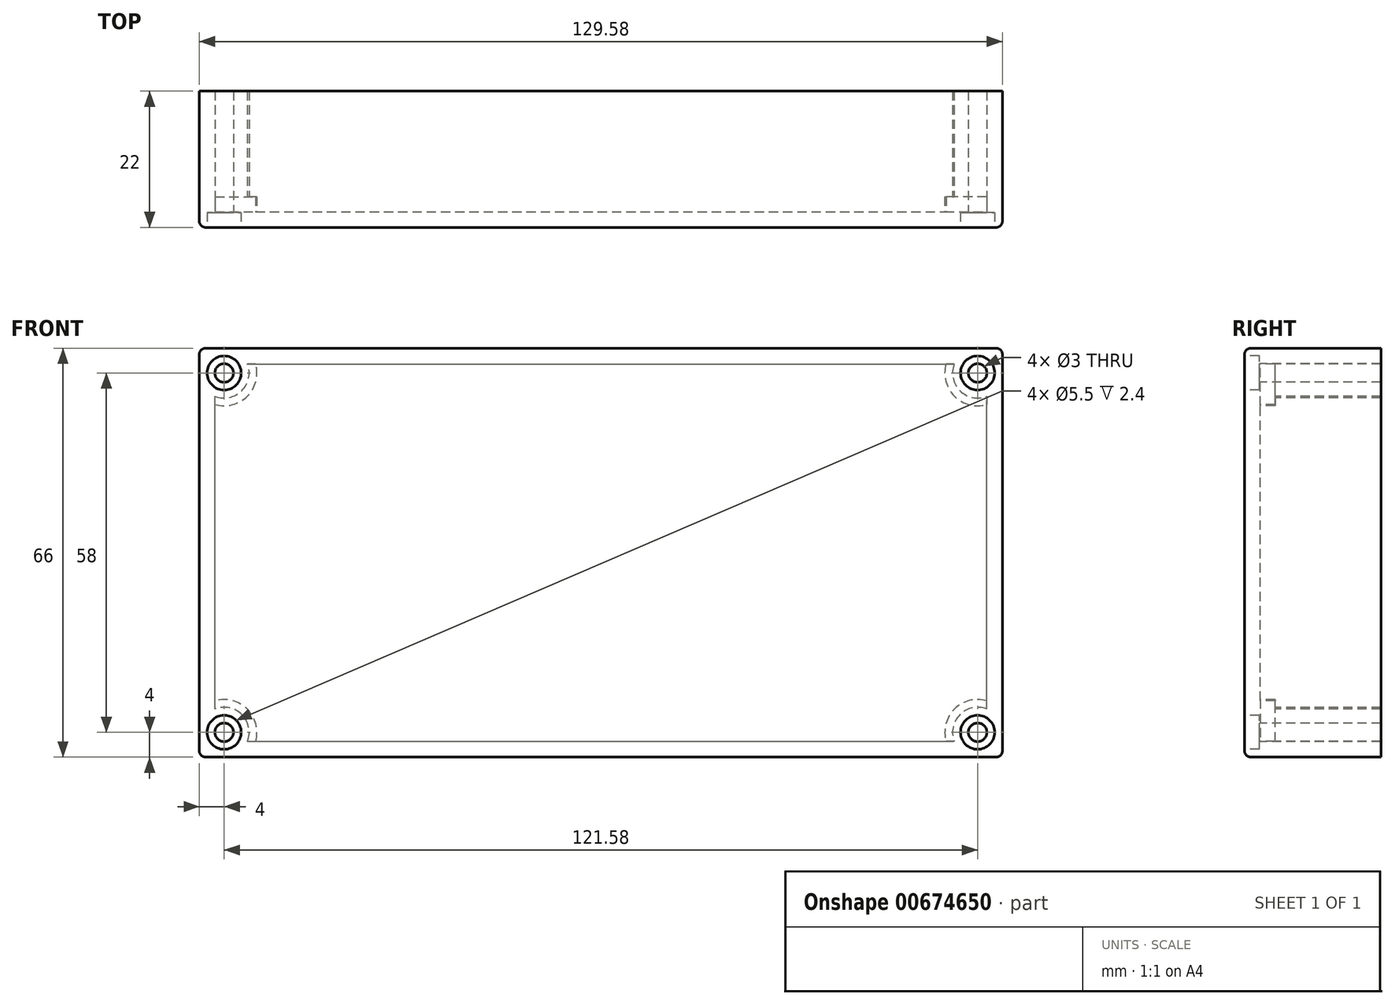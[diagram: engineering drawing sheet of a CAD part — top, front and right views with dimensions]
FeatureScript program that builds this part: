
annotation { "Feature Type Name" : "Feature", "Feature Type Description" : "" }
export const myFeature = defineFeature(function(context is Context, id is Id, definition is map)
    precondition{}
    {
        {
            var Q0;
            Q0=qCreatedBy(makeId("Front.planeOp"),FACE);
            var sketch = newSketch(context, id + "F0", { "sketchPlane" : qUnion([Q0])});
            skLineSegment(sketch, "E0.bottom", {"start": v(0, 0) * mm, "end": v(129.58, 0) * mm});
            skLineSegment(sketch, "E0.top", {"start": v(0, 66) * mm, "end": v(129.58, 66) * mm});
            skLineSegment(sketch, "E0.left", {"start": v(0, 0) * mm, "end": v(0, 66) * mm});
            skLineSegment(sketch, "E0.right", {"start": v(129.58, 0) * mm, "end": v(129.58, 66) * mm});
            skSolve(sketch);
        }
        {
            var Q0;
            Q0=makeQuery(id+"F0.imprint","IMPRINT",FACE,{"disambiguationData":[TD([[makeQuery(id+"F0.imprint","IMPRINT",EDGE,{"derivedFrom":sQuery(id+"F0.wireOp",EDGE,"E0.bottom")}),1.0]])]});
            extrude(context, id + "F1", {"entities" : qUnion([Q0]), "depth" : 22 * mm, "offsetDistance" : 25.4 * mm});
        }
        {
            var Q0;
            Q0=makeQuery(id+"F1.opExtrude","CAP_FACE",FACE,{"disambiguationData":[OSD([sQuery(id+"F0.wireOp",EDGE,"E0.bottom"),sQuery(id+"F0.wireOp",EDGE,"E0.top"),sQuery(id+"F0.wireOp",EDGE,"E0.left"),sQuery(id+"F0.wireOp",EDGE,"E0.right")])],"isStart":false});
            var sketch = newSketch(context, id + "F2", { "sketchPlane" : qUnion([Q0])});
            skCircle(sketch, "E1", {"center": v(4, 62) * mm, "radius": 1.5 * mm});
            skCircle(sketch, "E2", {"center": v(4, 4) * mm, "radius": 1.5 * mm});
            skCircle(sketch, "E3", {"center": v(125.58, 62) * mm, "radius": 1.5 * mm});
            skCircle(sketch, "E4", {"center": v(125.58, 4) * mm, "radius": 1.5 * mm});
            skSolve(sketch);
        }
        {
            var Q0;
            Q0=sQuery(id+"F2.wireOp",VERTEX,"E1.center");
            var Q1;
            Q1=sQuery(id+"F2.wireOp",VERTEX,"E2.center");
            var Q2;
            Q2=sQuery(id+"F2.wireOp",VERTEX,"E4.center");
            var Q3;
            Q3=sQuery(id+"F2.wireOp",VERTEX,"E3.center");
            var Q4;
            Q4=makeQuery(id+"F1.opExtrude","SWEPT_BODY",BODY,{"disambiguationData":[OSD([sQuery(id+"F0.wireOp",EDGE,"E0.bottom"),sQuery(id+"F0.wireOp",EDGE,"E0.top"),sQuery(id+"F0.wireOp",EDGE,"E0.left"),sQuery(id+"F0.wireOp",EDGE,"E0.right")])]});
            hole(context, id + "F3", {"style" : HoleStyle.C_BORE, "endStyle" : HoleEndStyle.THROUGH, "holeDiameter" : 3 * mm, "cBoreDiameter" : 5.5 * mm, "cBoreDepth" : 2.4 * mm, "majorDiameter" : 6.35 * mm, "isTappedThrough" : true, "tappedDepth" : 12.7 * mm, "tapClearance" : 3, "startFromSketch" : true, "locations" : qUnion([Q0, Q1, Q2, Q3]), "scope" : qUnion([Q4])});
        }
        {
            var Q0;
            Q0=makeQuery(id+"F1.opExtrude","CAP_FACE",FACE,{"disambiguationData":[OSD([sQuery(id+"F0.wireOp",EDGE,"E0.bottom"),sQuery(id+"F0.wireOp",EDGE,"E0.top"),sQuery(id+"F0.wireOp",EDGE,"E0.left"),sQuery(id+"F0.wireOp",EDGE,"E0.right")])],"isStart":true});
            shell(context, id + "F4", {"entities" : qUnion([Q0]), "thickness" : 2.54 * mm});
        }
        {
            var Q0;
            Q0=makeQuery(id+"F1.opExtrude","CAP_EDGE",EDGE,{"disambiguationData":[OSD([sQuery(id+"F0.wireOp",EDGE,"E0.top")])],"isStart":false});
            var Q1;
            Q1=makeQuery(id+"F1.opExtrude","SWEPT_EDGE",EDGE,{"disambiguationData":[OSD([sQuery(id+"F0.wireOp",EDGE,"E0.top"),sQuery(id+"F0.wireOp",EDGE,"E0.left")])]});
            var Q2;
            Q2=makeQuery(id+"F1.opExtrude","SWEPT_EDGE",EDGE,{"disambiguationData":[OSD([sQuery(id+"F0.wireOp",EDGE,"E0.bottom"),sQuery(id+"F0.wireOp",EDGE,"E0.left")])]});
            var Q3;
            Q3=makeQuery(id+"F1.opExtrude","SWEPT_EDGE",EDGE,{"disambiguationData":[OSD([sQuery(id+"F0.wireOp",EDGE,"E0.top"),sQuery(id+"F0.wireOp",EDGE,"E0.right")])]});
            var Q4;
            Q4=makeQuery(id+"F1.opExtrude","SWEPT_EDGE",EDGE,{"disambiguationData":[OSD([sQuery(id+"F0.wireOp",EDGE,"E0.bottom"),sQuery(id+"F0.wireOp",EDGE,"E0.right")])]});
            var Q5;
            Q5=makeQuery(id+"F1.opExtrude","CAP_EDGE",EDGE,{"disambiguationData":[OSD([sQuery(id+"F0.wireOp",EDGE,"E0.bottom")])],"isStart":false});
            var Q6;
            Q6=makeQuery(id+"F1.opExtrude","CAP_EDGE",EDGE,{"disambiguationData":[OSD([sQuery(id+"F0.wireOp",EDGE,"E0.right")])],"isStart":false});
            var Q7;
            Q7=makeQuery(id+"F1.opExtrude","CAP_EDGE",EDGE,{"disambiguationData":[OSD([sQuery(id+"F0.wireOp",EDGE,"E0.left")])],"isStart":false});
            fillet(context, id + "F5", {"entities" : qUnion([Q0, Q1, Q2, Q3, Q4, Q5, Q6, Q7]), "radius" : 1 * mm, "tangentPropagation" : true, "allowEdgeOverflow" : false});
        }
    });
